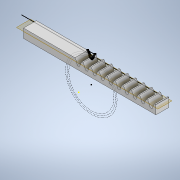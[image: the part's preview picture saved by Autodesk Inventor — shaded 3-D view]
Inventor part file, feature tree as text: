
AUTODESK INVENTOR PART (.ipt)
format: ipt  version: 2021 (Build 250183000, 183)  size: 168,448 bytes
history: native  units: mm
features: extrude x2, sketch x2, pattern_linear x1, plane x1
ambient origin geometry x8: Origin, YZ Plane, XZ Plane, XY Plane, X Axis, Y Axis, Z Axis, Center Point
bodies: Body1 (feature_tree)
feature tree (6):
  extrude  "Extrusion4"  Depth=7.0mm
  extrude  "Extrusion5"  Depth=10.0mm TaperAngle=0.0deg
  pattern_linear  "Rectangular Pattern1"  Spacing1=10.0mm  [1 undecoded]
  plane  "Work Plane1"
  sketch  "Sketch5"  dims[d12=40.0mm d13=10.0mm d14=0.0mm d15=10.0mm d16=0.0mm d17=150.0mm d19=6.285714mm d7=1.0mm d8=1.0mm d9=1.0mm d18=0.375mm]
  sketch  "Sketch4"  dims[d10=103.0mm d11=7.0mm]
note: 1 required parameter value undecoded (feature->parameter linkage not recoverable at this tier; creation-order binding heuristic only, values carry confidence <= 0.55)
